# Revit family: Accessory-Step_Stool-KOHLER-Stillness-K-31409_1
name_source: partatom
category: Specialty Equipment
revit_build: Autodesk Revit 2017 (Build: 20160225_1515(x64)
units: mm (PartAtom-declared; Revit-internal decimal feet)

## family parameters
Cut with Voids When Loaded = No
Host = Face
OmniClass Number = 23.31.25.00
OmniClass Title = Toilet and Bath Specialties
Part Type = Normal
Room Calculation Point = No
Round Connector Dimension = Use Diameter
Shared = No

## types (1)
- NA-Hinoki
    ADA Compliant = No
    Assembly Code = C1030200
    Date Modified = 12/04/2020
    Default Elevation = 0"
    Description = Step Stool
    Finish = KOHLER-Wood-NA-Hinoki
    Height = 10 1/8"
    Length = 12 1/2"
    Manufacturer = KOHLER Co.
    Master Format 2014 = 10 28 00
    Master Format 2014 Name = Toilet, Bath, and Laundry Accessories
    Material = Hinoki Wood
    Model = K-31409-NA
    Product Documentation Link = https://www.us.kohler.com
    Product Name = Stillness
    Product Page URL = http://www.us.kohler.com
    Type = 1
    URL = https://www.us.kohler.com
    WaterSense Certified = No
    Width = 22"

## geometry (parser evidence)
native form markers: Sweep x6
no freeform markers — native parametric forms only
